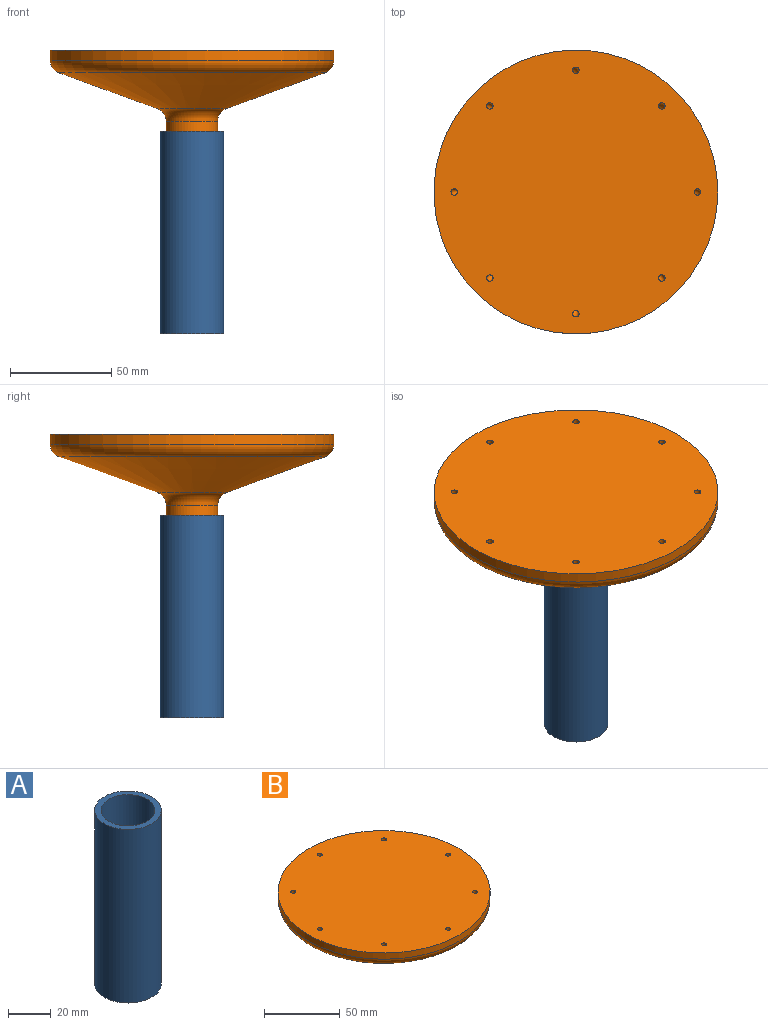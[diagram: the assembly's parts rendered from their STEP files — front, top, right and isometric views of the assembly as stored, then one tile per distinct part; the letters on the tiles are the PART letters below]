
ASSEMBLY  parts=2 mates=1
PART A: 4 faces, bbox 31.4x31.4x100 mm
  f0: cylinder r=12.7mm len=100mm, axis (0,0,-1), area 7979.6mm2, adj f2,f3
  f1: cylinder r=15.7mm len=100mm, axis (0,0,-1), area 9864.6mm2, adj f2,f3
  f2: plane 31.4x31.4mm, normal (0,0,1), area 267.7mm2, adj f0,f1
  f3: plane 31.4x31.4mm, normal (0,0,-1), area 267.7mm2, adj f0,f1
PART B: 47 faces, bbox 151.5x151.5x40 mm
  f0: cylinder r=70mm len=140mm, axis (0,0,1), area 2199.1mm2, adj f1,f6
  f1: plane 140x140mm, normal (0,0,1), area 15330.5mm2, adj f0,f7,f12,f17,f22,f27,f32,f37
  f2: plane 25.4x25.4mm, normal (0,0,-1), area 443.4mm2, adj f3,f11,f16,f21,f26,f31,f36,f41
  f3: cylinder r=12.7mm len=25.4mm, axis (0,0,1), area 399mm2, adj f2,f4
  f4: torus R=19.23mm, axis (0,0,1), area 712.2mm2, adj f3,f5
  f5: cone r=17mm half-angle=70deg, axis (0,0,1), area 13466.7mm2, adj f4,f6
  f6: torus R=63.47mm, axis (0,0,1), area 3433.2mm2, adj f0,f5
  f7: cylinder r=1.59mm len=5mm, axis (0,0,-1), area 49.9mm2, adj f1,f8
  f8: torus R=4.58mm, axis (0,1,0), area 55.9mm2, adj f7,f9
  f9: cylinder r=1.59mm len=42.68mm, axis (-0.94,0,-0.34), area 441.5mm2, adj f8,f10
  f10: torus R=11.23mm, axis (0,-1,0), area 136.8mm2, adj f9,f11
  f11: cylinder r=1.59mm len=5mm, axis (0,0,-1), area 49.9mm2, adj f2,f10
  f12: cylinder r=1.59mm len=5mm, axis (0,0,-1), area 49.9mm2, adj f1,f13
  f13: torus R=4.58mm, axis (-0.71,0.71,0), area 55.9mm2, adj f12,f14
  f14: cylinder r=1.59mm len=31.78mm, axis (-0.66,-0.66,-0.34), area 441.5mm2, adj f13,f15
  f15: torus R=11.23mm, axis (0.71,-0.71,0), area 136.8mm2, adj f14,f16
  f16: cylinder r=1.59mm len=5mm, axis (0,0,-1), area 49.9mm2, adj f2,f15
  f17: cylinder r=1.59mm len=5mm, axis (0,0,-1), area 49.9mm2, adj f1,f18
  f18: torus R=4.58mm, axis (-1,0,0), area 55.9mm2, adj f17,f19
  f19: cylinder r=1.59mm len=42.68mm, axis (0,-0.94,-0.34), area 441.5mm2, adj f18,f20
  f20: torus R=11.23mm, axis (1,0,0), area 136.8mm2, adj f19,f21
  f21: cylinder r=1.59mm len=5mm, axis (0,0,-1), area 49.9mm2, adj f2,f20
  f22: cylinder r=1.59mm len=5mm, axis (0,0,-1), area 49.9mm2, adj f1,f23
  f23: torus R=4.58mm, axis (-0.71,-0.71,0), area 55.9mm2, adj f22,f24
  f24: cylinder r=1.59mm len=31.78mm, axis (0.66,-0.66,-0.34), area 441.5mm2, adj f23,f25
  f25: torus R=11.23mm, axis (0.71,0.71,0), area 136.8mm2, adj f24,f26
  f26: cylinder r=1.59mm len=5mm, axis (0,0,-1), area 49.9mm2, adj f2,f25
  f27: cylinder r=1.59mm len=5mm, axis (0,0,-1), area 49.9mm2, adj f1,f28
  f28: torus R=4.58mm, axis (0,-1,0), area 55.9mm2, adj f27,f29
  f29: cylinder r=1.59mm len=42.68mm, axis (0.94,0,-0.34), area 441.5mm2, adj f28,f30
  f30: torus R=11.23mm, axis (0,1,0), area 136.8mm2, adj f29,f31
  f31: cylinder r=1.59mm len=5mm, axis (0,0,-1), area 49.9mm2, adj f2,f30
  f32: cylinder r=1.59mm len=5mm, axis (0,0,-1), area 49.9mm2, adj f1,f33
  f33: torus R=4.58mm, axis (0.71,-0.71,0), area 55.9mm2, adj f32,f34
  f34: cylinder r=1.59mm len=31.78mm, axis (0.66,0.66,-0.34), area 441.5mm2, adj f33,f35
  f35: torus R=11.23mm, axis (-0.71,0.71,0), area 136.8mm2, adj f34,f36
  f36: cylinder r=1.59mm len=5mm, axis (0,0,-1), area 49.9mm2, adj f2,f35
  f37: cylinder r=1.59mm len=5mm, axis (0,0,-1), area 49.9mm2, adj f1,f38
  f38: torus R=4.58mm, axis (1,0,0), area 55.9mm2, adj f37,f39
  f39: cylinder r=1.59mm len=42.68mm, axis (0,0.94,-0.34), area 441.5mm2, adj f38,f40
  f40: torus R=11.23mm, axis (-1,0,0), area 136.8mm2, adj f39,f41
  f41: cylinder r=1.59mm len=5mm, axis (0,0,-1), area 49.9mm2, adj f2,f40
  f42: cylinder r=1.59mm len=5mm, axis (0,0,-1), area 49.9mm2, adj f1,f43
  f43: torus R=4.58mm, axis (0.71,0.71,0), area 55.9mm2, adj f42,f44
  f44: cylinder r=1.59mm len=31.78mm, axis (-0.66,0.66,-0.34), area 441.5mm2, adj f43,f45
  f45: torus R=11.23mm, axis (-0.71,-0.71,0), area 136.8mm2, adj f44,f46
  f46: cylinder r=1.59mm len=5mm, axis (0,0,-1), area 49.9mm2, adj f2,f45
PLACE A t=(0,0,-100)mm
PLACE B at identity fixed
MATE fastened B.f0 <-> A.f0  axis (0,0,-1) through (0,0,0)mm
